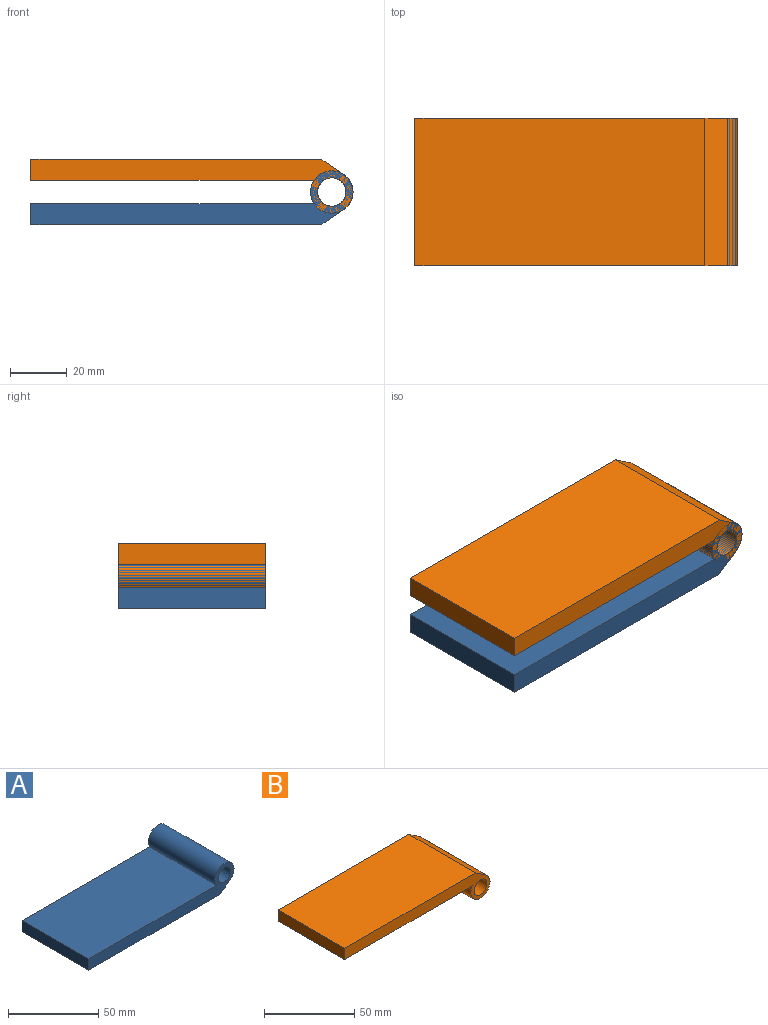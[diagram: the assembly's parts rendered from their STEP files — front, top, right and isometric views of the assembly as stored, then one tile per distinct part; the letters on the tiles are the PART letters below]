
ASSEMBLY  parts=2 mates=1
PART A: 8 faces, bbox 113.8x52.1x19.2 mm
  f0: plane 100x52.1mm, normal (0,0,1), area 5210mm2, adj f1,f5,f6,f7
  f1: plane 52.1x7.56mm, normal (-1,0,0), area 393.9mm2, adj f0,f2,f6,f7
  f2: plane 102.43x52.1mm, normal (0,0,-1), area 5336.9mm2, adj f1,f3,f6,f7
  f3: plane 52.1x8.05mm, normal (0.56,0,-0.83), area 506.3mm2, adj f2,f5,f6,f7
  f4: cylinder r=5mm len=52.1mm, axis (0,-1,0), area 1636.8mm2, adj f6,f7
  f5: cylinder r=7.5mm len=52.1mm, axis (0,-1,0), area 1834.8mm2, adj f0,f3,f6,f7
  f6: plane 113.78x19.16mm, normal (0,1,0), area 883.9mm2, adj f0,f1,f2,f3,f4,f5
  f7: plane 113.78x19.16mm, normal (0,-1,0), area 883.9mm2, adj f0,f1,f2,f3,f4,f5
PART B: 8 faces, bbox 113.8x52.1x19.2 mm
  f0: plane 100x52.1mm, normal (0,0,-1), area 5210mm2, adj f1,f5,f6,f7
  f1: plane 52.1x7.56mm, normal (-1,0,0), area 393.9mm2, adj f0,f2,f6,f7
  f2: plane 102.43x52.1mm, normal (0,0,1), area 5336.9mm2, adj f1,f3,f6,f7
  f3: plane 52.1x8.05mm, normal (0.56,0,0.83), area 506.3mm2, adj f2,f5,f6,f7
  f4: cylinder r=5mm len=52.1mm, axis (0,-1,0), area 1636.8mm2, adj f6,f7
  f5: cylinder r=7.5mm len=52.1mm, axis (0,-1,0), area 1834.8mm2, adj f0,f3,f6,f7
  f6: plane 113.78x19.16mm, normal (0,1,0), area 883.9mm2, adj f0,f1,f2,f3,f4,f5
  f7: plane 113.78x19.16mm, normal (0,-1,0), area 883.9mm2, adj f0,f1,f2,f3,f4,f5
PLACE A t=(-4.32,-16.63,18.18)mm
PLACE B t=(-4.32,-16.63,-32.63)mm
MATE revolute B.f4 <-> A.f4  axis (0,-1,0) through (39.65,-16.63,22.27)mm
